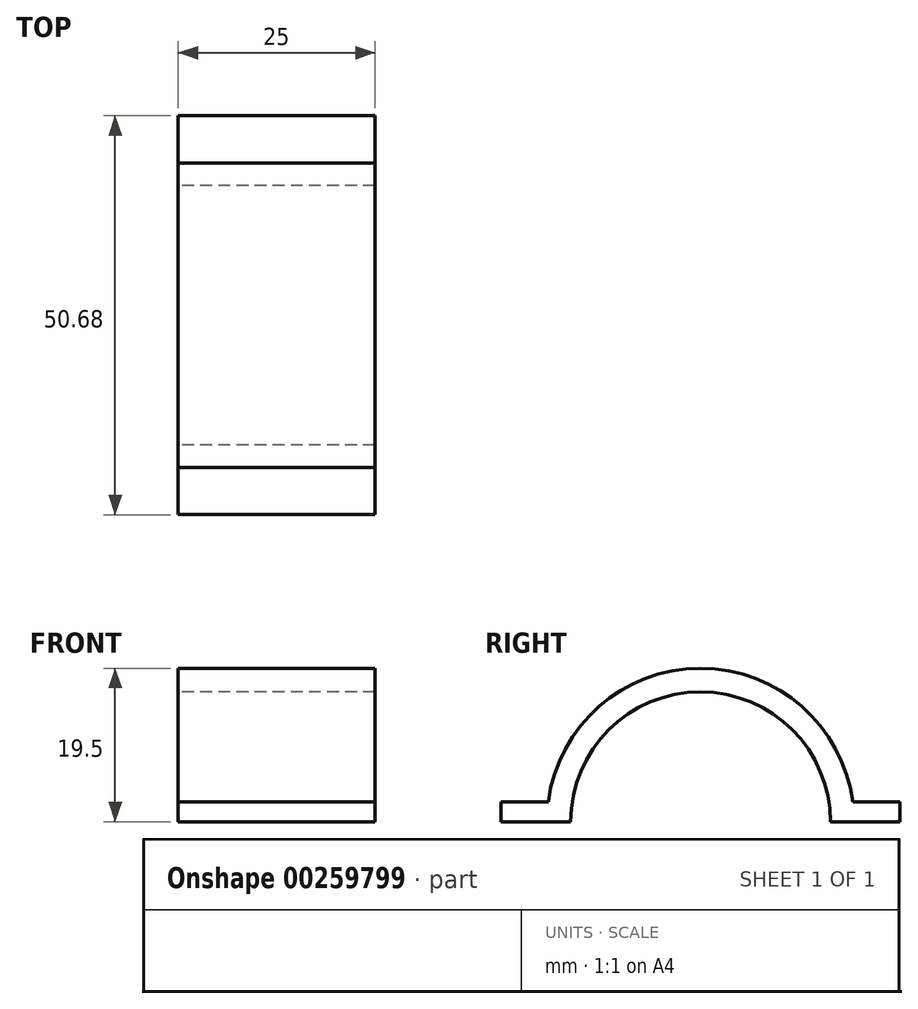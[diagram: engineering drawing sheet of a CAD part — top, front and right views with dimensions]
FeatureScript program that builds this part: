
annotation { "Feature Type Name" : "Feature", "Feature Type Description" : "" }
export const myFeature = defineFeature(function(context is Context, id is Id, definition is map)
    precondition{}
    {
        {
            var Q0;
            Q0=qCreatedBy(makeId("Right.planeOp"),FACE);
            var sketch = newSketch(context, id + "F0", { "sketchPlane" : qUnion([Q0])});
            skLineSegment(sketch, "E0", {"start": v(-25.34, 2.5) * mm, "end": v(-19.34, 2.5) * mm});
            skArc(sketch, "E1", {"start": v(16.5, 0) * mm, "mid": v(0, 16.5) * mm, "end": v(-16.5, 0) * mm});
            skPoint(sketch, "E2.trimOffspring.end.orphan", {"position": v(11.87, 2.5) * mm});
            skPoint(sketch, "E3.start.orphan", {"position": v(11.87, -2.5) * mm});
            skLineSegment(sketch, "E4", {"start": v(19.34, 2.5) * mm, "end": v(25.34, 2.5) * mm});
            skLineSegment(sketch, "E5", {"start": v(25.34, 2.5) * mm, "end": v(25.34, 0) * mm});
            skLineSegment(sketch, "E6", {"start": v(16.5, 0) * mm, "end": v(25.34, 0) * mm});
            skPoint(sketch, "E7.orphan", {"position": v(16.3, 2.5) * mm});
            skArc(sketch, "E8.trimOffspring", {"start": v(19.34, 2.5) * mm, "mid": v(0, 19.5) * mm, "end": v(-19.34, 2.5) * mm});
            skPoint(sketch, "E9.orphan", {"position": v(16.3, -2.5) * mm});
            skLineSegment(sketch, "E10", {"start": v(-16.5, 0) * mm, "end": v(-25.34, 0) * mm});
            skLineSegment(sketch, "E11", {"start": v(-25.34, 0) * mm, "end": v(-25.34, 2.5) * mm});
            skPoint(sketch, "E12.end.orphan", {"position": v(25.34, -2.5) * mm});
            skPoint(sketch, "E13.end.orphan", {"position": v(-32.34, -2.5) * mm});
            skSolve(sketch);
        }
        {
            var Q0;
            Q0 = qSketchRegion(id + "F0", true);
            extrude(context, id + "F1", {"entities" : qUnion([Q0]), "depth" : 25 * mm, "offsetDistance" : 25 * mm});
        }
    });
